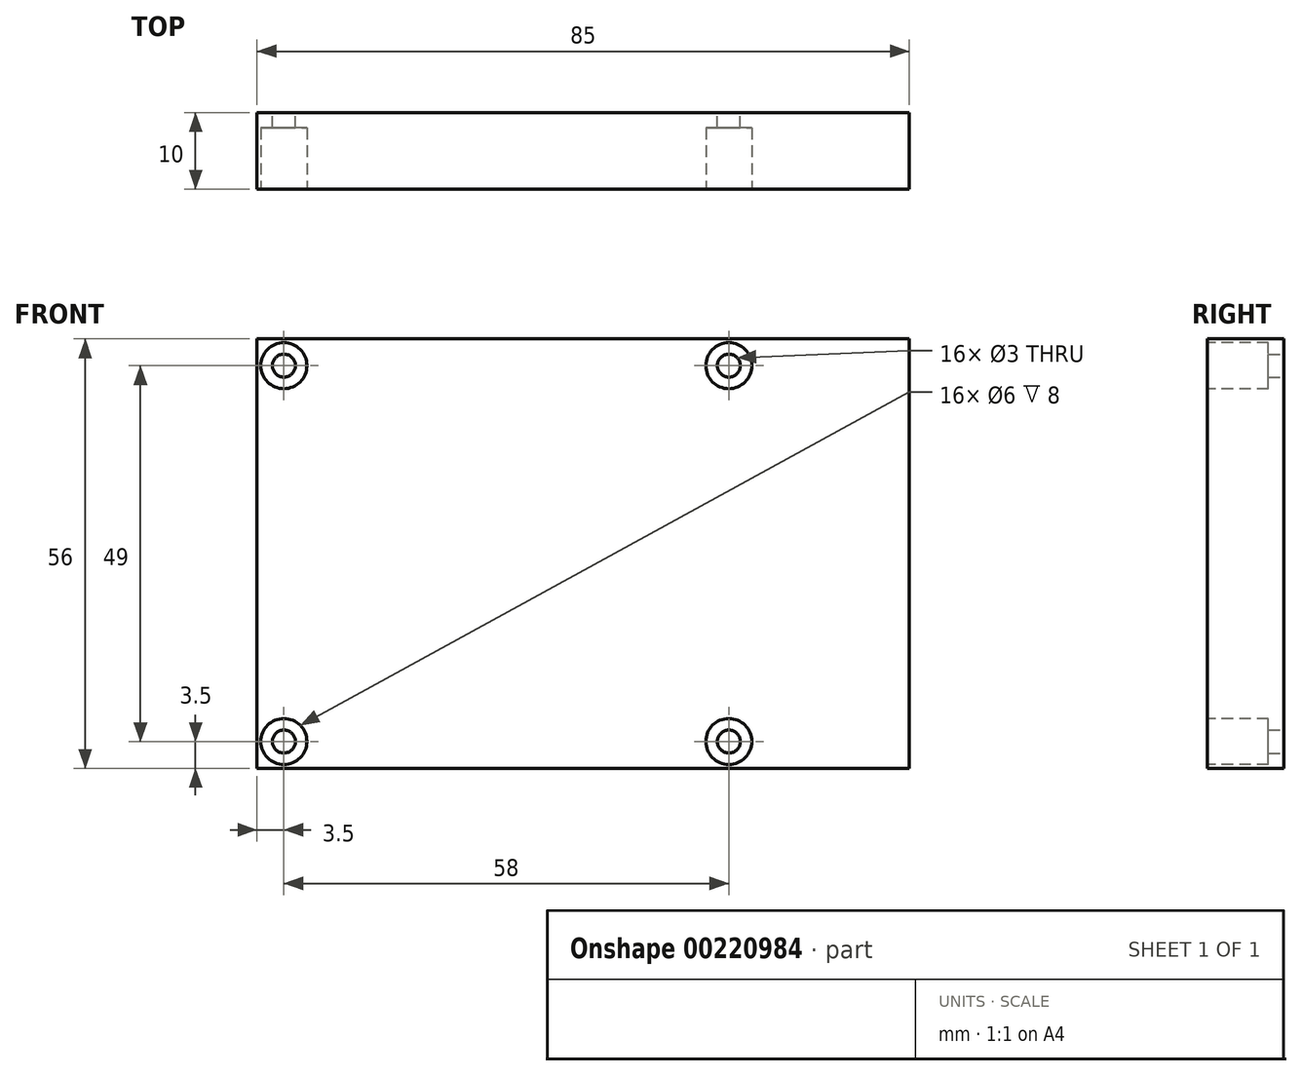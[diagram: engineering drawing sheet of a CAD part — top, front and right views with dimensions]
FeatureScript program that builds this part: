
annotation { "Feature Type Name" : "Feature", "Feature Type Description" : "" }
export const myFeature = defineFeature(function(context is Context, id is Id, definition is map)
    precondition{}
    {
        {
            var Q0;
            Q0=qCreatedBy(makeId("Front.planeOp"),FACE);
            var sketch = newSketch(context, id + "F0", { "sketchPlane" : qUnion([Q0])});
            skLineSegment(sketch, "E0.bottom", {"start": v(42.5, 28) * mm, "end": v(-42.5, 28) * mm});
            skLineSegment(sketch, "E0.top", {"start": v(42.5, -28) * mm, "end": v(-42.5, -28) * mm});
            skLineSegment(sketch, "E0.left", {"start": v(42.5, 28) * mm, "end": v(42.5, -28) * mm});
            skLineSegment(sketch, "E0.right", {"start": v(-42.5, 28) * mm, "end": v(-42.5, -28) * mm});
            skPoint(sketch, "E0.middle", {"position": v(0, 0) * mm});
            skLineSegment(sketch, "E1", {"start": v(-42.5, -28) * mm, "end": v(-39, -28) * mm});
            skLineSegment(sketch, "E2", {"start": v(-39, -28) * mm, "end": v(-39, -24.5) * mm});
            skLineSegment(sketch, "E3", {"start": v(-42.5, 28) * mm, "end": v(-39, 28) * mm});
            skLineSegment(sketch, "E4", {"start": v(-39, 28) * mm, "end": v(-39, 24.5) * mm});
            skCircle(sketch, "E5", {"center": v(-39, 24.5) * mm, "radius": 1.5 * mm});
            skCircle(sketch, "E6", {"center": v(-39, -24.5) * mm, "radius": 1.5 * mm});
            skLineSegment(sketch, "E7", {"start": v(-39, 24.5) * mm, "end": v(19, 24.5) * mm});
            skCircle(sketch, "E8", {"center": v(19, 24.5) * mm, "radius": 1.5 * mm});
            skLineSegment(sketch, "E9", {"start": v(-39, -24.5) * mm, "end": v(19, -24.5) * mm});
            skCircle(sketch, "E10", {"center": v(19, -24.5) * mm, "radius": 1.5 * mm});
            skLineSegment(sketch, "E11", {"start": v(19, 24.5) * mm, "end": v(42.5, 24.5) * mm});
            skSolve(sketch);
        }
        {
            var Q0;
            Q0 = qSketchRegion(id + "F0", true);
            extrude(context, id + "F1", {"entities" : qUnion([Q0]), "depth" : 10 * mm});
        }
        {
            var Q0;
            Q0=makeQuery(id+"F1.opExtrude","CAP_FACE",FACE,{"disambiguationData":[OSD([sQuery(id+"F0.wireOp",EDGE,"E0.bottom"),sQuery(id+"F0.wireOp",EDGE,"E0.top"),sQuery(id+"F0.wireOp",EDGE,"E0.left"),sQuery(id+"F0.wireOp",EDGE,"E0.right"),sQuery(id+"F0.wireOp",EDGE,"E1"),sQuery(id+"F0.wireOp",EDGE,"E3"),sQuery(id+"F0.wireOp",EDGE,"E5"),sQuery(id+"F0.wireOp",EDGE,"E6"),sQuery(id+"F0.wireOp",EDGE,"E8"),sQuery(id+"F0.wireOp",EDGE,"E10")])],"isStart":false});
            var sketch = newSketch(context, id + "F2", { "sketchPlane" : qUnion([Q0])});
            skCircle(sketch, "E12", {"center": v(-39, 24.5) * mm, "radius": 3 * mm});
            skCircle(sketch, "E13", {"center": v(19, 24.5) * mm, "radius": 3 * mm});
            skCircle(sketch, "E14", {"center": v(19, -24.5) * mm, "radius": 3 * mm});
            skCircle(sketch, "E15", {"center": v(-39, -24.5) * mm, "radius": 3 * mm});
            skSolve(sketch);
        }
        {
            var Q0;
            Q0 = qSketchRegion(id + "F2", true);
            extrude(context, id + "F3", {"entities" : qUnion([Q0]), "operationType" : NewBodyOperationType.REMOVE, "oppositeDirection" : true, "depth" : 8 * mm});
        }
    });
